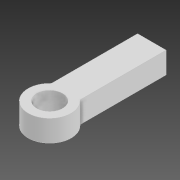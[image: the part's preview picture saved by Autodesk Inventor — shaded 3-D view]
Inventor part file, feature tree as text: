
AUTODESK INVENTOR PART (.ipt)
format: ipt  version: 2020 (Build 240168000, 168)  size: 91,136 bytes
history: native  units: in
note: dims shown in document units (in); Inventor stores cm internally (conversion verified against a paired STEP export)
features: extrude x2, sketch x2
ambient origin geometry x8: Origin, YZ Plane, XZ Plane, XY Plane, X Axis, Y Axis, Z Axis, Center Point
bodies: Solid1 (feature_tree)
feature tree (4):
  extrude  "Extrusion1"  Depth=0.3937in
  extrude  "Extrusion2"  Depth=0.1969in
  sketch  "Sketch1"  dims[d0=0.2362in d1=0.3937in]
  sketch  "Sketch2"  dims[d2=0.1969in d3=0.0in d4=0.7874in d5=0.1969in d6=0.0in]
